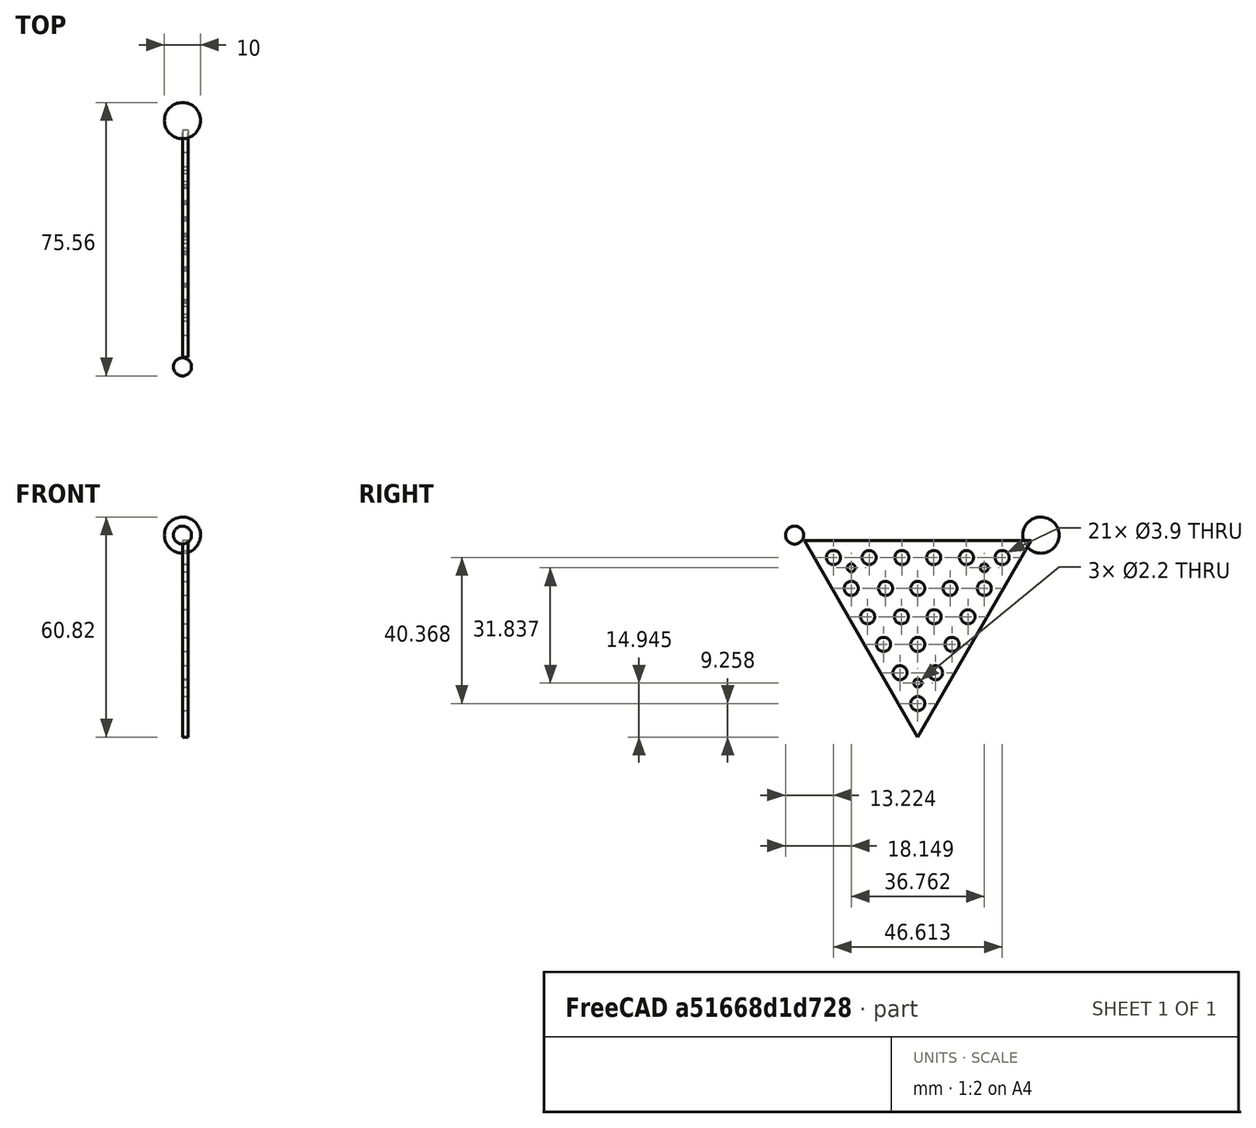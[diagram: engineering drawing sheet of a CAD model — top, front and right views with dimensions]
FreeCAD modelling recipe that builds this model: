
FCSTD DOCUMENT  (FreeCAD 0.19R24267 +99 (Git))
Label: isocahedron2
License: All rights reserved
LicenseURL: http://en.wikipedia.org/wiki/All_rights_reserved
objects: Part::Part2DObjectPython×23, Part::Feature×4, Sketcher::SketchObject×1
note: 28 computed .brp shape members not serialized (recipe doc carries the construction recipe); baked Part::Feature solids carry a one-line shape summary decoded from their .brp

FEATURE [Part::Part2DObjectPython] Line  # Draft 2D object (typed FeaturePython)
  Area = 0
  ChamferSize = 0
  Closed = false
  End = (-64.0444,29.0183,16.7537)
  FilletRadius = 0
  Length = 72.2803
  MakeFace = true
  Points = (2) [(0,0,0),(-64.0444,29.0183,16.7537)]
  Start = (0,0,0)
  Subdivisions = 0
FEATURE [Part::Part2DObjectPython] Line001  # Draft 2D object (typed FeaturePython)
  Area = 0
  ChamferSize = 0
  Closed = false
  End = (-67.79,17.7334,17.7336)
  FilletRadius = 0
  Length = 72.2803
  MakeFace = true
  Points = (2) [(0,0,0),(-67.79,17.7334,17.7336)]
  Start = (0,0,0)
  Subdivisions = 0
FEATURE [Part::Part2DObjectPython] Line002  # Draft 2D object (typed FeaturePython)
  Area = 0
  ChamferSize = 0
  Closed = false
  End = (-69.6887,5.9653,18.2302)
  FilletRadius = 0
  Length = 72.2803
  MakeFace = true
  Points = (2) [(0,0,0),(-69.6887,5.9653,18.2302)]
  Start = (0,0,0)
  Subdivisions = 0
FEATURE [Part::Part2DObjectPython] Line003  # Draft 2D object (typed FeaturePython)
  Area = 0
  ChamferSize = 0
  Closed = false
  End = (-69.6887,-5.9653,18.2302)
  FilletRadius = 0
  Length = 72.2803
  MakeFace = true
  Points = (2) [(0,0,0),(-69.6887,-5.9653,18.2302)]
  Start = (0,0,0)
  Subdivisions = 0
FEATURE [Part::Part2DObjectPython] Line004  # Draft 2D object (typed FeaturePython)
  Area = 0
  ChamferSize = 0
  Closed = false
  End = (-67.79,-17.7334,17.7336)
  FilletRadius = 0
  Length = 72.2803
  MakeFace = true
  Points = (2) [(0,0,0),(-67.79,-17.7334,17.7336)]
  Start = (0,0,0)
  Subdivisions = 0
FEATURE [Part::Part2DObjectPython] Line005  # Draft 2D object (typed FeaturePython)
  Area = 0
  ChamferSize = 0
  Closed = false
  End = (-64.0444,-29.0183,16.7537)
  FilletRadius = 0
  Length = 72.2803
  MakeFace = true
  Points = (2) [(0,0,0),(-64.0444,-29.0183,16.7537)]
  Start = (0,0,0)
  Subdivisions = 0
FEATURE [Part::Part2DObjectPython] Line006  # Draft 2D object (typed FeaturePython)
  Area = 0
  ChamferSize = 0
  Closed = false
  End = (-67.79,24.2244,6.49078)
  FilletRadius = 0
  Length = 72.2803
  MakeFace = true
  Points = (2) [(0,0,0),(-67.79,24.2244,6.49078)]
  Start = (0,0,0)
  Subdivisions = 0
FEATURE [Part::Part2DObjectPython] Line007  # Draft 2D object (typed FeaturePython)
  Area = 0
  ChamferSize = 0
  Closed = false
  End = (-70.9033,12.2912,6.78887)
  FilletRadius = 0
  Length = 72.2803
  MakeFace = true
  Points = (2) [(0,0,0),(-70.9033,12.2912,6.78887)]
  Start = (0,0,0)
  Subdivisions = 0
FEATURE [Part::Part2DObjectPython] Line008  # Draft 2D object (typed FeaturePython)
  Area = 0
  ChamferSize = 0
  Closed = false
  End = (-71.9512,-1.36e-14,6.8892)
  FilletRadius = 0
  Length = 72.2803
  MakeFace = true
  Points = (2) [(0,0,0),(-71.9512,-1.3628e-14,6.8892)]
  Start = (0,0,0)
  Subdivisions = 0
FEATURE [Part::Part2DObjectPython] Line009  # Draft 2D object (typed FeaturePython)
  Area = 0
  ChamferSize = 0
  Closed = false
  End = (-70.9033,-12.2912,6.78887)
  FilletRadius = 0
  Length = 72.2803
  MakeFace = true
  Points = (2) [(0,0,0),(-70.9033,-12.2912,6.78887)]
  Start = (0,0,0)
  Subdivisions = 0
FEATURE [Part::Part2DObjectPython] Line010  # Draft 2D object (typed FeaturePython)
  Area = 0
  ChamferSize = 0
  Closed = false
  End = (-67.79,-24.2244,6.49078)
  FilletRadius = 0
  Length = 72.2803
  MakeFace = true
  Points = (2) [(0,0,0),(-67.79,-24.2244,6.49078)]
  Start = (0,0,0)
  Subdivisions = 0
FEATURE [Part::Part2DObjectPython] Line011  # Draft 2D object (typed FeaturePython)
  Area = 0
  ChamferSize = 0
  Closed = false
  End = (-69.6887,18.7705,-3.94902)
  FilletRadius = 0
  Length = 72.2803
  MakeFace = true
  Points = (2) [(0,0,0),(-69.6887,18.7705,-3.94902)]
  Start = (0,0,0)
  Subdivisions = 0
FEATURE [Part::Part2DObjectPython] Line012  # Draft 2D object (typed FeaturePython)
  Area = 0
  ChamferSize = 0
  Closed = false
  End = (-71.888,6.3213,-4.07365)
  FilletRadius = 0
  Length = 72.2803
  MakeFace = true
  Points = (2) [(0,0,0),(-71.888,6.3213,-4.07365)]
  Start = (0,0,0)
  Subdivisions = 0
FEATURE [Part::Part2DObjectPython] Line013  # Draft 2D object (typed FeaturePython)
  Area = 0
  ChamferSize = 0
  Closed = false
  End = (-71.888,-6.3213,-4.07365)
  FilletRadius = 0
  Length = 72.2803
  MakeFace = true
  Points = (2) [(0,0,0),(-71.888,-6.3213,-4.07365)]
  Start = (0,0,0)
  Subdivisions = 0
FEATURE [Part::Part2DObjectPython] Line014  # Draft 2D object (typed FeaturePython)
  Area = 0
  ChamferSize = 0
  Closed = false
  End = (-69.6887,-18.7705,-3.94902)
  FilletRadius = 0
  Length = 72.2803
  MakeFace = true
  Points = (2) [(0,0,0),(-69.6887,-18.7705,-3.94902)]
  Start = (0,0,0)
  Subdivisions = 0
FEATURE [Part::Part2DObjectPython] Line015  # Draft 2D object (typed FeaturePython)
  Area = 0
  ChamferSize = 0
  Closed = false
  End = (-69.6887,12.8052,-14.2812)
  FilletRadius = 0
  Length = 72.2803
  MakeFace = true
  Points = (2) [(0,0,0),(-69.6887,12.8052,-14.2812)]
  Start = (0,0,0)
  Subdivisions = 0
FEATURE [Part::Part2DObjectPython] Line016  # Draft 2D object (typed FeaturePython)
  Area = 0
  ChamferSize = 0
  Closed = false
  End = (-70.8088,3.9e-15,-14.5108)
  FilletRadius = 0
  Length = 72.2803
  MakeFace = true
  Points = (2) [(0,0,0),(-70.8088,3.88578e-15,-14.5108)]
  Start = (0,0,0)
  Subdivisions = 0
FEATURE [Part::Part2DObjectPython] Line017  # Draft 2D object (typed FeaturePython)
  Area = 0
  ChamferSize = 0
  Closed = false
  End = (-69.6887,-12.8052,-14.2812)
  FilletRadius = 0
  Length = 72.2803
  MakeFace = true
  Points = (2) [(0,0,0),(-69.6887,-12.8052,-14.2812)]
  Start = (0,0,0)
  Subdivisions = 0
FEATURE [Part::Part2DObjectPython] Line018  # Draft 2D object (typed FeaturePython)
  Area = 0
  ChamferSize = 0
  Closed = false
  End = (-67.79,6.49102,-24.2243)
  FilletRadius = 0
  Length = 72.2803
  MakeFace = true
  Points = (2) [(0,0,0),(-67.79,6.49102,-24.2243)]
  Start = (0,0,0)
  Subdivisions = 0
FEATURE [Part::Part2DObjectPython] Line019  # Draft 2D object (typed FeaturePython)
  Area = 0
  ChamferSize = 0
  Closed = false
  End = (-67.79,-6.49102,-24.2243)
  FilletRadius = 0
  Length = 72.2803
  MakeFace = true
  Points = (2) [(0,0,0),(-67.79,-6.49102,-24.2243)]
  Start = (0,0,0)
  Subdivisions = 0
FEATURE [Part::Part2DObjectPython] Line020  # Draft 2D object (typed FeaturePython)
  Area = 0
  ChamferSize = 0
  Closed = false
  End = (-64.0444,-1.39e-14,-33.5075)
  FilletRadius = 0
  Length = 72.2803
  MakeFace = true
  Points = (2) [(0,0,0),(-64.0444,-1.38778e-14,-33.5075)]
  Start = (0,0,0)
  Subdivisions = 0
FEATURE [Part::Feature] Shape
  Placement = pos=(-51.4379,34.0305,19.6475) rot=(0,0,1;0rad)
  shape: bbox 10 x 10 x 10 mm, 1 faces (baked)
FEATURE [Part::Feature] Shape001
  Placement = pos=(-51.4379,-34.0305,19.6475) rot=(0,0,1;0rad)
  shape: bbox 5 x 5 x 5 mm, 1 faces (baked)
FEATURE [Part::Part2DObjectPython] Line021  # Draft 2D object (typed FeaturePython)
  Area = 0
  ChamferSize = 0
  Closed = false
  End = (-57.4379,0,6.2e-15)
  FilletRadius = 0
  Length = 57.4379
  MakeFace = true
  Points = (2) [(0,0,0),(-57.4379,0,6.20075e-15)]
  Start = (0,0,0)
  Subdivisions = 0
FEATURE [Part::Feature] Shape002
  shape: bbox 24.38 x 79.76 x 69.75 mm, 137 faces (baked)
FEATURE [Part::Feature] Shape003
  shape: bbox 1.6 x 62.65 x 54.25 mm, 29 faces (baked)
FEATURE [Part::Part2DObjectPython] Shape2DView  # Draft 2D object (typed FeaturePython)
  Base = -> Shape002
  FuseArch = false
  HiddenLines = false
  InPlace = true
  Projection = (1,0,0)
  ProjectionMode = 0
  SegmentLength = 0.05
  Tessellation = false
  VisibleOnly = false
FEATURE [Sketcher::SketchObject] Sketch  label="Sketch_converted"
  FullyConstrained = false
  sketch-geometry (156):
    g0: ArcOfEllipse CenterX=1.99e-14 CenterY=-3.45e-14 CenterZ=0 NormalX=0 NormalY=0 NormalZ=1 MajorRadius=72.2803 MinorRadius=25.7912 AngleXU=-2.61799 StartAngle=4.15881 EndAngle=5.26596
    g1: ArcOfEllipse CenterX=0 CenterY=0 CenterZ=0 NormalX=0 NormalY=0 NormalZ=1 MajorRadius=72.2803 MinorRadius=25.7912 AngleXU=-0.523599 StartAngle=4.15881 EndAngle=5.26596
    g2: ArcOfEllipse CenterX=0 CenterY=0 CenterZ=0 NormalX=0 NormalY=0 NormalZ=1 MajorRadius=72.2803 MinorRadius=25.7912 AngleXU=1.5708 StartAngle=4.15881 EndAngle=5.26596
    g3: ArcOfEllipse CenterX=-24.1616 CenterY=-6.4742 CenterZ=0 NormalX=0 NormalY=0 NormalZ=1 MajorRadius=5.2 MinorRadius=4.87696 AngleXU=1.8326 StartAngle=4.14488 EndAngle=4.19554
    g4: ArcOfEllipse CenterX=-24.1616 CenterY=-6.4742 CenterZ=0 NormalX=0 NormalY=0 NormalZ=1 MajorRadius=5.2 MinorRadius=4.87696 AngleXU=1.8326 StartAngle=5.03807 EndAngle=5.07205
    g5: LineSegment StartX=19.6475 StartY=34.0305 StartZ=0 EndX=21.9393 EndY=38 EndZ=0
    g6: LineSegment StartX=-39.295 StartY=0 StartZ=0 EndX=-43.8786 EndY=0 EndZ=0
    g7: LineSegment StartX=-39.295 StartY=-5.68e-14 StartZ=0 EndX=19.6475 EndY=34.0305 EndZ=0
    g8: LineSegment StartX=21.9393 StartY=-38 StartZ=0 EndX=19.6475 EndY=-34.0305 EndZ=0
    g9: LineSegment StartX=19.6475 StartY=-34.0305 StartZ=0 EndX=-39.295 EndY=0 EndZ=0
    g10: LineSegment StartX=19.6475 StartY=34.0305 StartZ=0 EndX=19.6475 EndY=-34.0305 EndZ=0
    g11: LineSegment StartX=-28.6047 StartY=-2.95 StartZ=0 EndX=-28.6047 EndY=2.95 EndZ=0
    g12: LineSegment StartX=-28.6047 StartY=-2.95 StartZ=0 EndX=-25.2189 EndY=-2.95 EndZ=0
    g13: LineSegment StartX=-28.6047 StartY=2.95 StartZ=0 EndX=-25.2189 EndY=2.95 EndZ=0
    g14: LineSegment StartX=-25.2189 StartY=-2.95 StartZ=0 EndX=-25.2189 EndY=2.95 EndZ=0
    g15: LineSegment StartX=-20.4259 StartY=2.28488 StartZ=0 EndX=-19.4858 EndY=8.11322 EndZ=0
    g16: LineSegment StartX=-20.4259 StartY=2.28488 StartZ=0 EndX=-17.2762 EndY=1.73733 EndZ=0
    g17: LineSegment StartX=-19.4858 StartY=8.11322 StartZ=0 EndX=-16.3361 EndY=7.56567 EndZ=0
    g18: LineSegment StartX=-17.2762 StartY=1.73733 StartZ=0 EndX=-16.3361 EndY=7.56567 EndZ=0
    g19: Circle CenterX=-21.2246 CenterY=9.3e-15 CenterZ=0 NormalX=0 NormalY=0 NormalZ=-1 AngleXU=-3.14159 Radius=1.6
    g20: LineSegment StartX=-13.5813 StartY=8.09525 StartZ=0 EndX=-9.9403 EndY=12.739 EndZ=0
    g21: LineSegment StartX=-13.5813 StartY=8.09525 StartZ=0 EndX=-11.1419 EndY=6.1643 EndZ=0
    g22: LineSegment StartX=-9.9403 StartY=12.739 StartZ=0 EndX=-7.50093 EndY=10.808 EndZ=0
    g23: LineSegment StartX=-11.1419 StartY=6.1643 StartZ=0 EndX=-7.50093 EndY=10.808 EndZ=0
    g24: LineSegment StartX=-12.0723 StartY=-2.95 StartZ=0 EndX=-12.0723 EndY=2.95 EndZ=0
    g25: LineSegment StartX=-12.0723 StartY=-2.95 StartZ=0 EndX=-9.00993 EndY=-2.95 EndZ=0
    g26: LineSegment StartX=-12.0723 StartY=2.95 StartZ=0 EndX=-9.00993 EndY=2.95 EndZ=0
    g27: LineSegment StartX=-9.00993 StartY=-2.95 StartZ=0 EndX=-9.00993 EndY=2.95 EndZ=0
    g28: LineSegment StartX=-6.17823 StartY=14.5051 StartZ=0 EndX=-0.522641 EndY=16.1906 EndZ=0
    g29: LineSegment StartX=-6.17823 StartY=14.5051 StartZ=0 EndX=-5.30697 EndY=11.5188 EndZ=0
    g30: LineSegment StartX=-0.522641 StartY=16.1906 StartZ=0 EndX=0.348623 EndY=13.2042 EndZ=0
    g31: LineSegment StartX=-5.30697 StartY=11.5188 StartZ=0 EndX=0.348623 EndY=13.2042 EndZ=0
    g32: LineSegment StartX=7.28612 StartY=15.9881 StartZ=0 EndX=1.64283 EndY=17.711 EndZ=0
    g33: LineSegment StartX=7.28612 StartY=15.9881 StartZ=0 EndX=8.20734 EndY=19.0511 EndZ=0
    g34: LineSegment StartX=1.64283 StartY=17.711 StartZ=0 EndX=2.56405 EndY=20.774 EndZ=0
    g35: LineSegment StartX=8.20734 StartY=19.0511 StartZ=0 EndX=2.56405 EndY=20.774 EndZ=0
    g36: LineSegment StartX=15.0983 StartY=20.3188 StartZ=0 EndX=10.0636 EndY=23.3955 EndZ=0
    g37: LineSegment StartX=15.0983 StartY=20.3188 StartZ=0 EndX=16.8482 EndY=23.2171 EndZ=0
    g38: LineSegment StartX=10.0636 StartY=23.3955 StartZ=0 EndX=11.8135 EndY=26.2938 EndZ=0
    g39: LineSegment StartX=16.8482 StartY=23.2171 StartZ=0 EndX=11.8135 EndY=26.2938 EndZ=0
    g40: Circle CenterX=10.6123 CenterY=18.381 CenterZ=0 NormalX=0 NormalY=0 NormalZ=-1 AngleXU=-3.14159 Radius=1.6
    g41: LineSegment StartX=14.3262 StartY=10.21 StartZ=0 EndX=10.27 EndY=14.495 EndZ=0
    g42: LineSegment StartX=14.3262 StartY=10.21 StartZ=0 EndX=16.6418 EndY=12.4166 EndZ=0
    g43: LineSegment StartX=10.27 StartY=14.495 StartZ=0 EndX=12.5856 EndY=16.7015 EndZ=0
    g44: LineSegment StartX=16.6418 StartY=12.4166 StartZ=0 EndX=12.5856 EndY=16.7015 EndZ=0
    g45: LineSegment StartX=6.64574 StartY=6.07156 StartZ=0 EndX=1.61278 EndY=9.15082 EndZ=0
    g46: LineSegment StartX=6.64574 StartY=6.07156 StartZ=0 EndX=8.23739 EndY=8.68287 EndZ=0
    g47: LineSegment StartX=1.61278 StartY=9.15082 StartZ=0 EndX=3.20443 EndY=11.7621 EndZ=0
    g48: LineSegment StartX=8.23739 StartY=8.68287 StartZ=0 EndX=3.20443 EndY=11.7621 EndZ=0
    g49: LineSegment StartX=-6.19032 StartY=4.02961 StartZ=0 EndX=-1.39604 EndY=7.46847 EndZ=0
    g50: LineSegment StartX=-6.19032 StartY=4.02961 StartZ=0 EndX=-4.43357 EndY=1.57765 EndZ=0
    g51: LineSegment StartX=-1.39604 StartY=7.46847 StartZ=0 EndX=0.360711 EndY=5.01652 EndZ=0
    g52: LineSegment StartX=-4.43357 StartY=1.57765 StartZ=0 EndX=0.360711 EndY=5.01652 EndZ=0
    g53: LineSegment StartX=3.41822 StartY=-2.95 StartZ=0 EndX=3.41822 EndY=2.95 EndZ=0
    g54: LineSegment StartX=3.41822 StartY=-2.95 StartZ=0 EndX=6.43194 EndY=-2.95 EndZ=0
    g55: LineSegment StartX=3.41822 StartY=2.95 StartZ=0 EndX=6.43194 EndY=2.95 EndZ=0
    g56: LineSegment StartX=6.43194 StartY=-2.95 StartZ=0 EndX=6.43194 EndY=2.95 EndZ=0
    g57: LineSegment StartX=12.8518 StartY=1.12179 StartZ=0 EndX=11.0911 EndY=6.75298 EndZ=0
    g58: LineSegment StartX=12.8518 StartY=1.12179 StartZ=0 EndX=15.8207 EndY=2.05311 EndZ=0
    g59: LineSegment StartX=11.0911 StartY=6.75298 StartZ=0 EndX=14.06 EndY=7.6843 EndZ=0
    g60: LineSegment StartX=15.8207 StartY=2.05311 StartZ=0 EndX=14.06 EndY=7.6843 EndZ=0
    g61: LineSegment StartX=-19.4858 StartY=-8.11322 StartZ=0 EndX=-20.4259 EndY=-2.28488 EndZ=0
    g62: LineSegment StartX=-19.4858 StartY=-8.11322 StartZ=0 EndX=-16.3361 EndY=-7.56567 EndZ=0
    g63: LineSegment StartX=-20.4259 StartY=-2.28488 StartZ=0 EndX=-17.2762 EndY=-1.73733 EndZ=0
    g64: LineSegment StartX=-16.3361 StartY=-7.56567 StartZ=0 EndX=-17.2762 EndY=-1.73733 EndZ=0
    g65: LineSegment StartX=-9.9403 StartY=-12.739 StartZ=0 EndX=-13.5813 EndY=-8.09525 EndZ=0
    g66: LineSegment StartX=-9.9403 StartY=-12.739 StartZ=0 EndX=-7.50093 EndY=-10.808 EndZ=0
    g67: LineSegment StartX=-13.5813 StartY=-8.09525 StartZ=0 EndX=-11.1419 EndY=-6.1643 EndZ=0
    g68: LineSegment StartX=-7.50093 StartY=-10.808 StartZ=0 EndX=-11.1419 EndY=-6.1643 EndZ=0
    g69: LineSegment StartX=-1.39604 StartY=-7.46847 StartZ=0 EndX=-6.19032 EndY=-4.02961 EndZ=0
    g70: LineSegment StartX=-1.39604 StartY=-7.46847 StartZ=0 EndX=0.360711 EndY=-5.01652 EndZ=0
    g71: LineSegment StartX=-6.19032 StartY=-4.02961 StartZ=0 EndX=-4.43357 EndY=-1.57765 EndZ=0
    g72: LineSegment StartX=0.360711 StartY=-5.01652 StartZ=0 EndX=-4.43357 EndY=-1.57765 EndZ=0
    g73: LineSegment StartX=1.61278 StartY=-9.15082 StartZ=0 EndX=6.64574 EndY=-6.07156 EndZ=0
    g74: LineSegment StartX=1.61278 StartY=-9.15082 StartZ=0 EndX=3.20443 EndY=-11.7621 EndZ=0
    g75: LineSegment StartX=6.64574 StartY=-6.07156 StartZ=0 EndX=8.23739 EndY=-8.68287 EndZ=0
    g76: LineSegment StartX=3.20443 StartY=-11.7621 StartZ=0 EndX=8.23739 EndY=-8.68287 EndZ=0
    g77: LineSegment StartX=11.0911 StartY=-6.75298 StartZ=0 EndX=12.8518 EndY=-1.12179 EndZ=0
    g78: LineSegment StartX=11.0911 StartY=-6.75298 StartZ=0 EndX=14.06 EndY=-7.6843 EndZ=0
    g79: LineSegment StartX=12.8518 StartY=-1.12179 StartZ=0 EndX=15.8207 EndY=-2.05311 EndZ=0
    g80: LineSegment StartX=14.06 StartY=-7.6843 StartZ=0 EndX=15.8207 EndY=-2.05311 EndZ=0
    g81: LineSegment StartX=-0.522641 StartY=-16.1906 StartZ=0 EndX=-6.17823 EndY=-14.5051 EndZ=0
    g82: LineSegment StartX=-0.522641 StartY=-16.1906 StartZ=0 EndX=0.348623 EndY=-13.2042 EndZ=0
    g83: LineSegment StartX=-6.17823 StartY=-14.5051 StartZ=0 EndX=-5.30697 EndY=-11.5188 EndZ=0
    g84: LineSegment StartX=0.348623 StartY=-13.2042 StartZ=0 EndX=-5.30697 EndY=-11.5188 EndZ=0
    g85: LineSegment StartX=1.64283 StartY=-17.711 StartZ=0 EndX=7.28612 EndY=-15.9881 EndZ=0
    g86: LineSegment StartX=1.64283 StartY=-17.711 StartZ=0 EndX=2.56405 EndY=-20.774 EndZ=0
    g87: LineSegment StartX=7.28612 StartY=-15.9881 StartZ=0 EndX=8.20734 EndY=-19.0511 EndZ=0
    g88: LineSegment StartX=2.56405 StartY=-20.774 StartZ=0 EndX=8.20734 EndY=-19.0511 EndZ=0
    g89: Circle CenterX=10.6123 CenterY=-18.381 CenterZ=0 NormalX=0 NormalY=0 NormalZ=-1 AngleXU=-3.14159 Radius=1.6
    g90: LineSegment StartX=10.27 StartY=-14.495 StartZ=0 EndX=14.3262 EndY=-10.21 EndZ=0
    g91: LineSegment StartX=10.27 StartY=-14.495 StartZ=0 EndX=12.5856 EndY=-16.7015 EndZ=0
    g92: LineSegment StartX=14.3262 StartY=-10.21 StartZ=0 EndX=16.6418 EndY=-12.4166 EndZ=0
    g93: LineSegment StartX=12.5856 StartY=-16.7015 StartZ=0 EndX=16.6418 EndY=-12.4166 EndZ=0
    g94: LineSegment StartX=10.0636 StartY=-23.3955 StartZ=0 EndX=15.0983 EndY=-20.3188 EndZ=0
    g95: LineSegment StartX=10.0636 StartY=-23.3955 StartZ=0 EndX=11.8135 EndY=-26.2938 EndZ=0
    g96: LineSegment StartX=15.0983 StartY=-20.3188 StartZ=0 EndX=16.8482 EndY=-23.2171 EndZ=0
    g97: LineSegment StartX=11.8135 StartY=-26.2938 StartZ=0 EndX=16.8482 EndY=-23.2171 EndZ=0
    g98: LineSegment StartX=-28.0062 StartY=2.95 StartZ=0 EndX=-28.0062 EndY=-2.95 EndZ=0
    g99: LineSegment StartX=-20.381 StartY=-2.56312 StartZ=0 EndX=-20.3233 EndY=-2.55381 EndZ=0
    g100: LineSegment StartX=-20.3233 StartY=-2.55381 StartZ=0 EndX=-19.3606 EndY=-8.09146 EndZ=0
    g101: LineSegment StartX=-13.4779 StartY=-8.22707 StartZ=0 EndX=-13.1954 EndY=-8.00557 EndZ=0
    g102: LineSegment StartX=-13.1954 StartY=-8.00557 StartZ=0 EndX=-9.63798 EndY=-12.4997 EndZ=0
    g103: LineSegment StartX=-11.2345 StartY=2.95 StartZ=0 EndX=-11.2345 EndY=-2.95 EndZ=0
    g104: LineSegment StartX=-19.3606 StartY=8.09146 StartZ=0 EndX=-20.3233 EndY=2.55381 EndZ=0
    g105: LineSegment StartX=-20.381 StartY=2.56312 StartZ=0 EndX=-20.3233 EndY=2.55381 EndZ=0
    g106: LineSegment StartX=-9.63798 StartY=12.4997 StartZ=0 EndX=-13.1954 EndY=8.00557 EndZ=0
    g107: LineSegment StartX=-13.4779 StartY=8.22707 StartZ=0 EndX=-13.1954 EndY=8.00557 EndZ=0
    g108: LineSegment StartX=-5.97795 StartY=-14.5648 StartZ=0 EndX=-5.87547 EndY=-14.221 EndZ=0
    g109: LineSegment StartX=-5.87547 StartY=-14.221 StartZ=0 EndX=-0.41295 EndY=-15.8146 EndZ=0
    g110: LineSegment StartX=8.09659 StartY=-19.0129 StartZ=0 EndX=2.53727 EndY=-20.6849 EndZ=0
    g111: LineSegment StartX=8.09659 StartY=-19.0129 StartZ=0 EndX=8.1167 EndY=-19.0788 EndZ=0
    g112: LineSegment StartX=-6.14228 StartY=-4.06407 StartZ=0 EndX=-5.09488 EndY=-2.60383 EndZ=0
    g113: LineSegment StartX=-5.09488 StartY=-2.60383 StartZ=0 EndX=-0.347591 EndY=-6.00512 EndZ=0
    g114: LineSegment StartX=7.69447 StartY=-7.97028 StartZ=0 EndX=2.73553 EndY=-10.9929 EndZ=0
    g115: LineSegment StartX=7.69447 StartY=-7.97028 StartZ=0 EndX=8.15958 EndY=-8.73048 EndZ=0
    g116: LineSegment StartX=4.53822 StartY=2.95 StartZ=0 EndX=4.53822 EndY=-2.95 EndZ=0
    g117: LineSegment StartX=16.4998 StartY=-22.7462 StartZ=0 EndX=11.4957 EndY=-25.7675 EndZ=0
    g118: LineSegment StartX=16.4998 StartY=-22.7462 StartZ=0 EndX=16.804 EndY=-23.2441 EndZ=0
    g119: LineSegment StartX=16.5387 StartY=-12.4226 StartZ=0 EndX=12.5205 EndY=-16.6394 EndZ=0
    g120: LineSegment StartX=16.5387 StartY=-12.4226 StartZ=0 EndX=16.5901 EndY=-12.4712 EndZ=0
    g121: LineSegment StartX=15.4629 StartY=-1.9762 StartZ=0 EndX=13.7071 EndY=-7.57359 EndZ=0
    g122: LineSegment StartX=15.4629 StartY=-1.9762 StartZ=0 EndX=15.8108 EndY=-2.08495 EndZ=0
    g123: LineSegment StartX=-0.347591 StartY=6.00512 StartZ=0 EndX=-5.09488 EndY=2.60383 EndZ=0
    g124: LineSegment StartX=-6.14228 StartY=4.06407 StartZ=0 EndX=-5.09488 EndY=2.60383 EndZ=0
    g125: LineSegment StartX=2.73553 StartY=10.9929 StartZ=0 EndX=7.69447 EndY=7.97028 EndZ=0
    g126: LineSegment StartX=7.69447 StartY=7.97028 StartZ=0 EndX=8.15958 EndY=8.73048 EndZ=0
    g127: LineSegment StartX=-0.41295 StartY=15.8146 StartZ=0 EndX=-5.87547 EndY=14.221 EndZ=0
    g128: LineSegment StartX=-5.97795 StartY=14.5648 StartZ=0 EndX=-5.87547 EndY=14.221 EndZ=0
    g129: LineSegment StartX=2.53727 StartY=20.6849 StartZ=0 EndX=8.09659 EndY=19.0129 EndZ=0
    g130: LineSegment StartX=8.09659 StartY=19.0129 StartZ=0 EndX=8.1167 EndY=19.0788 EndZ=0
    g131: LineSegment StartX=13.7071 StartY=7.57359 StartZ=0 EndX=15.4629 EndY=1.9762 EndZ=0
    g132: LineSegment StartX=15.4629 StartY=1.9762 StartZ=0 EndX=15.8108 EndY=2.08495 EndZ=0
    g133: LineSegment StartX=12.5205 StartY=16.6394 StartZ=0 EndX=16.5387 EndY=12.4226 EndZ=0
    g134: LineSegment StartX=16.5387 StartY=12.4226 StartZ=0 EndX=16.5901 EndY=12.4712 EndZ=0
    g135: LineSegment StartX=11.4957 StartY=25.7675 StartZ=0 EndX=16.4998 EndY=22.7462 EndZ=0
    g136: LineSegment StartX=16.4998 StartY=22.7462 StartZ=0 EndX=16.804 EndY=23.2441 EndZ=0
    g137: LineSegment StartX=-17.2762 StartY=1.73733 StartZ=0 EndX=-20.3233 EndY=2.55381 EndZ=0
    g138: LineSegment StartX=-11.1419 StartY=6.1643 StartZ=0 EndX=-13.1954 EndY=8.00557 EndZ=0
    g139: LineSegment StartX=-5.30697 StartY=11.5188 StartZ=0 EndX=-5.87547 EndY=14.221 EndZ=0
    g140: LineSegment StartX=7.28612 StartY=15.9881 StartZ=0 EndX=8.09659 EndY=19.0129 EndZ=0
    g141: LineSegment StartX=15.0983 StartY=20.3188 StartZ=0 EndX=16.4998 EndY=22.7462 EndZ=0
    g142: LineSegment StartX=14.3262 StartY=10.21 StartZ=0 EndX=16.5387 EndY=12.4226 EndZ=0
    g143: LineSegment StartX=6.64574 StartY=6.07156 StartZ=0 EndX=7.69447 EndY=7.97028 EndZ=0
    g144: LineSegment StartX=-4.43357 StartY=1.57765 StartZ=0 EndX=-5.09488 EndY=2.60383 EndZ=0
    g145: LineSegment StartX=12.8518 StartY=1.12179 StartZ=0 EndX=15.4629 EndY=1.9762 EndZ=0
    g146: LineSegment StartX=-17.2762 StartY=-1.73733 StartZ=0 EndX=-20.3233 EndY=-2.55381 EndZ=0
    g147: LineSegment StartX=-11.1419 StartY=-6.1643 StartZ=0 EndX=-13.1954 EndY=-8.00557 EndZ=0
    g148: LineSegment StartX=-4.43357 StartY=-1.57765 StartZ=0 EndX=-5.09488 EndY=-2.60383 EndZ=0
    g149: LineSegment StartX=6.64574 StartY=-6.07156 StartZ=0 EndX=7.69447 EndY=-7.97028 EndZ=0
    g150: LineSegment StartX=12.8518 StartY=-1.12179 StartZ=0 EndX=15.4629 EndY=-1.9762 EndZ=0
    g151: LineSegment StartX=-5.30697 StartY=-11.5188 StartZ=0 EndX=-5.87547 EndY=-14.221 EndZ=0
    g152: LineSegment StartX=7.28612 StartY=-15.9881 StartZ=0 EndX=8.09659 EndY=-19.0129 EndZ=0
    g153: LineSegment StartX=14.3262 StartY=-10.21 StartZ=0 EndX=16.5387 EndY=-12.4226 EndZ=0
    g154: LineSegment StartX=15.0983 StartY=-20.3188 StartZ=0 EndX=16.4998 EndY=-22.7462 EndZ=0
    g155: LineSegment StartX=-28.0062 StartY=1.64e-14 StartZ=0 EndX=-28.6047 EndY=1.67e-14 EndZ=0
